# Revit family: ee1490ff-0ed9-4a4a-aa33-30f9202c20b6
name_source: partatom
category: Casework
revit_build: Autodesk Revit 2018 (Build: 20180423_1000(x64)
units: mm (PartAtom-declared; Revit-internal decimal feet)

## family parameters
Cut with Voids When Loaded = No
Host = Face
OmniClass Number = 23.40.35.17.47.14
OmniClass Title = Bathroom Casework
Room Calculation Point = No
Shared = No

## types (1)
- Not a Type - See Type Catalog
    ADA Compliant = No
    Assembly Code = E2010
    Construction Type = Wall-Mount
    Date Modified = 05/31/2018
    Default Elevation = 35"
    Depth = 21 7/8"
    Hardware Included = No
    Height = 19"
    Left drawer vanity = No
    Manufacturer = KOHLER Co.
    MasterFormat 1995 = 08715
    MasterFormat 2004 = 08.71.73
    Material = Solid wood and veneers
    Product Documentation Link = http://www.us.kohler.com
    Product Finish = Default
    Product Name = Damask
    Product Page URL = http://www.us.kohler.com
    Right drawer vanity = No
    Type = 0
    URL = https://www.us.kohler.com
    Width = 30"

## geometry (parser evidence)
native form markers: Sweep x3
no freeform markers — native parametric forms only
